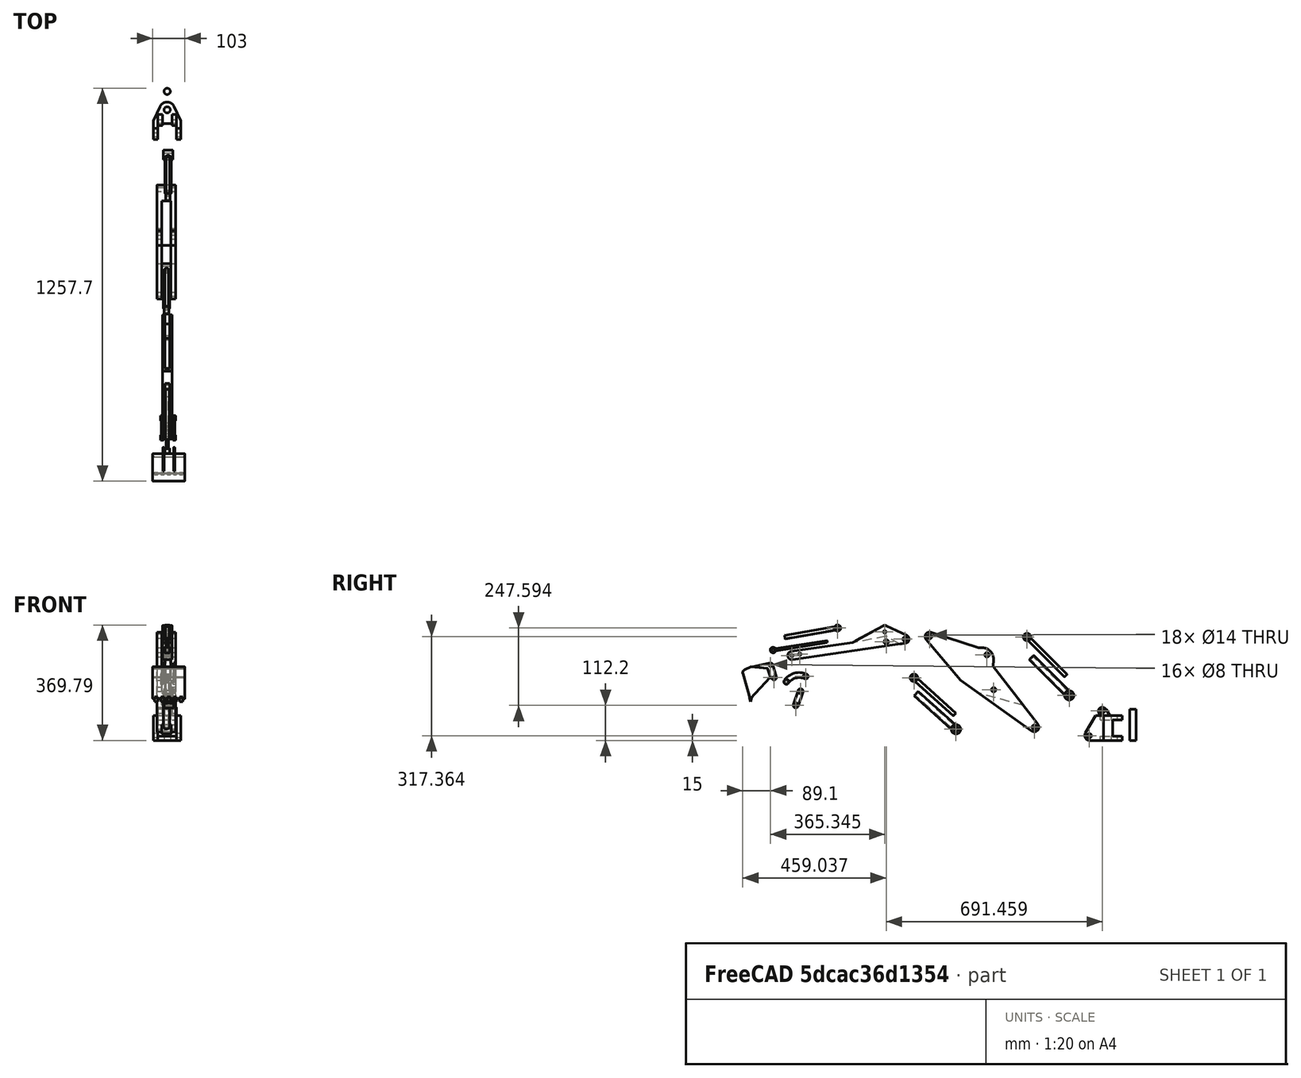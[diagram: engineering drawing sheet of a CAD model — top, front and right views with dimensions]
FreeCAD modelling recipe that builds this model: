
FCSTD DOCUMENT  (FreeCAD 1.0R39319 (Git))
Label: brazo-hidraulico
License: CC-BY 4.0
LicenseURL: https://creativecommons.org/licenses/by/4.0/
objects: App::FeaturePython×17, Part::Feature×13, App::Link×13, App::DocumentObjectGroup×1, Assembly::JointGroup×1, Assembly::AssemblyObject×1
note: 13 computed .brp shape members not serialized (recipe doc carries the construction recipe); baked Part::Feature solids carry a one-line shape summary decoded from their .brp

FEATURE [Part::Feature] Shape001  label="Base"
  shape: bbox 88 x 119.5 x 106 mm, 44 faces (baked)
FEATURE [Part::Feature] Shape012  label="BasePin"
  shape: bbox 20 x 20 x 100 mm, 3 faces (baked)
FEATURE [Part::Feature] Shape013  label="Stick"
  shape: bbox 30 x 388.4 x 109.8 mm, 24 faces (baked)
FEATURE [Part::Feature] Shape014  label="BucketLink1"
  shape: bbox 30 x 31.36 x 61.47 mm, 22 faces (baked)
FEATURE [Part::Feature] Shape015  label="Bucket"
  shape: bbox 103 x 108.6 x 124 mm, 97 faces (baked)
FEATURE [Part::Feature] Shape016  label="BoomCylinderInner"
  shape: bbox 15 x 140.2 x 140.2 mm, 6 faces (baked)
FEATURE [Part::Feature] Shape017  label="StickCylinderInner"
  shape: bbox 15 x 146.3 x 133.8 mm, 6 faces (baked)
FEATURE [Part::Feature] Shape018  label="BucketCylinderInner"
  shape: bbox 15 x 182.7 x 39.88 mm, 6 faces (baked)
FEATURE [Part::Feature] Shape019  label="BucketLink2"
  shape: bbox 48 x 78 x 37.57 mm, 23 faces (baked)
FEATURE [Part::Feature] Shape020  label="BoomCylinderOuter"
  shape: bbox 30 x 143 x 143 mm, 8 faces (baked)
FEATURE [Part::Feature] Shape021  label="StickCylinderOuter"
  shape: bbox 30 x 148.8 x 136.9 mm, 8 faces (baked)
FEATURE [Part::Feature] Shape022  label="BucketCylinderOuter"
  shape: bbox 15 x 179.4 x 45.6 mm, 10 faces (baked)
FEATURE [Part::Feature] Shape  label="Boom"
  shape: bbox 60 x 364 x 319 mm, 31 faces (baked)
FEATURE [App::DocumentObjectGroup] Group  label="CAD"
  Group = -> [Shape001,Shape012,Shape013,Shape014,Shape015,Shape016,Shape017,Shape018,Shape019,Shape020,Shape021,Shape022,Shape]
FEATURE [App::Link] BasePin  label="BasePin001"
  LinkPlacement = pos=(-206.517,40.2557,364.268) rot=(0,0,1;0rad)
  LinkedObject = -> Shape012
  Placement = pos=(-206.517,40.2557,364.268) rot=(0,0,1;0rad)
FEATURE [App::Link] Base  label="Base001"
  LinkPlacement = pos=(-206.517,99.4157,364.268) rot=(0,0,-1;0.004633rad)
  LinkedObject = -> Shape001
  Placement = pos=(-206.517,99.4157,364.268) rot=(0,0,-1;0.004633rad)
FEATURE [App::Link] Boom  label="Boom001"
  LinkPlacement = pos=(-202.932,230.97,229.247) rot=(-0.999947,0.002316,-0.010058;0.452746rad)
  LinkedObject = -> Shape
  Placement = pos=(-202.932,230.97,229.247) rot=(-0.999947,0.002316,-0.010058;0.452746rad)
FEATURE [App::Link] Stick  label="Stick001"
  LinkPlacement = pos=(-205.469,390.408,208.421) rot=(-0.999934,0.002316,-0.011244;0.406359rad)
  LinkedObject = -> Shape013
  Placement = pos=(-205.469,390.408,208.421) rot=(-0.999934,0.002316,-0.011244;0.406359rad)
FEATURE [App::Link] Bucket  label="Bucket001"
  LinkPlacement = pos=(-210.075,432.194,196.62) rot=(-0.99995,0.002316,-0.009747;0.466683rad)
  LinkedObject = -> Shape015
  Placement = pos=(-210.075,432.194,196.62) rot=(-0.99995,0.002316,-0.009747;0.466683rad)
FEATURE [App::Link] BucketLink2  label="BucketLink003"
  LinkPlacement = pos=(-215.535,-1246.73,276.477) rot=(0.999997,-0.002316,0.001009;3.9632rad)
  LinkedObject = -> Shape019
  Placement = pos=(-215.535,-1246.73,276.477) rot=(0.999997,-0.002316,0.001009;3.9632rad)
FEATURE [App::Link] BucketLink1  label="BucketLink004"
  LinkPlacement = pos=(-212.089,-2.4321,-20.3863) rot=(-0.999989,0.002316,-0.004149;1.01849rad)
  LinkedObject = -> Shape014
  Placement = pos=(-212.089,-2.4321,-20.3863) rot=(-0.999989,0.002316,-0.004149;1.01849rad)
FEATURE [App::Link] BoomCylinderOuter  label="BoomCylinderOuter001"
  LinkPlacement = pos=(-209.106,136.254,268.963) rot=(-0.999935,0.002316,-0.011152;0.409629rad)
  LinkedObject = -> Shape020
  Placement = pos=(-209.106,136.254,268.963) rot=(-0.999935,0.002316,-0.011152;0.409629rad)
FEATURE [App::Link] BoomCylinderInner  label="BoomCylinderInner001"
  LinkPlacement = pos=(-208.727,108.582,238.805) rot=(-0.999935,0.002316,-0.011152;0.409629rad)
  LinkedObject = -> Shape016
  Placement = pos=(-208.727,108.582,238.805) rot=(-0.999935,0.002316,-0.011152;0.409629rad)
FEATURE [App::Link] StickCylinderInner  label="StickCylinderInner001"
  LinkPlacement = pos=(-203.709,310.952,236.711) rot=(-0.999971,0.002316,-0.007276;0.616456rad)
  LinkedObject = -> Shape017
  Placement = pos=(-203.709,310.952,236.711) rot=(-0.999971,0.002316,-0.007276;0.616456rad)
FEATURE [App::Link] StickCylinderOuter  label="StickCylinderOuter001"
  LinkPlacement = pos=(-203.027,347.623,221.922) rot=(-0.999971,0.002316,-0.007276;0.616456rad)
  LinkedObject = -> Shape021
  Placement = pos=(-203.027,347.623,221.922) rot=(-0.999971,0.002316,-0.007276;0.616456rad)
FEATURE [App::Link] BucketCylinderInner  label="BucketCylinderInner001"
  LinkPlacement = pos=(-205.355,395.972,110.555) rot=(-0.999962,0.002316,-0.008436;0.535995rad)
  LinkedObject = -> Shape018
  Placement = pos=(-205.355,395.972,110.555) rot=(-0.999962,0.002316,-0.008436;0.535995rad)
FEATURE [App::Link] BucketCylinderOuter  label="BucketCylinderOuter001"
  LinkPlacement = pos=(-205.403,417.48,46.5045) rot=(-0.999964,0.002316,-0.008156;0.553448rad)
  LinkedObject = -> Shape022
  Placement = pos=(-205.403,417.48,46.5045) rot=(-0.999964,0.002316,-0.008156;0.553448rad)
FEATURE [App::FeaturePython] GroundedJoint  # Assembly grounded joint (typed FeaturePython)
  ObjectToGround = -> BasePin
  Placement = pos=(-206.517,40.2557,364.268) rot=(0,0,1;0rad)
FEATURE [App::FeaturePython] Revolute  # Assembly joint (typed FeaturePython)
  Activated = true
  AngleMax = 0
  AngleMin = 0
  Detach1 = false
  Detach2 = false
  Distance = 0
  Distance2 = 0
  EnableAngleMax = false
  EnableAngleMin = false
  EnableLengthMax = false
  EnableLengthMin = false
  JointType = 1 (Revolute)
  LengthMax = 0
  LengthMin = 0
  Placement1 = pos=(0,59.16,0) rot=(0,0,1;1.5708rad)
  Placement2 = pos=(0,0,0) rot=(0.707107,0.707107,0;3.14159rad)
  Reference1 = -> Assembly [BasePin.Face1,BasePin.Edge2]
  Reference2 = -> Assembly [Base.Edge107,Base.Edge107]
FEATURE [App::FeaturePython] Revolute001  # Assembly joint (typed FeaturePython)
  Activated = true
  AngleMax = 45
  AngleMin = -45
  Detach1 = false
  Detach2 = false
  Distance = 0
  Distance2 = 0
  EnableAngleMax = true
  EnableAngleMin = true
  EnableLengthMax = false
  EnableLengthMin = false
  JointType = 1 (Revolute)
  LengthMax = 0
  LengthMin = 0
  Placement1 = pos=(-32.9758,-255.877,42.3644) rot=(0.57735,0.57735,0.57735;2.0944rad)
  Placement2 = pos=(-30,-80,15) rot=(-0.57735,-0.57735,0.57735;2.0944rad)
  Reference1 = -> Assembly [Boom.Face1,Boom.Edge5]
  Reference2 = -> Assembly [Base.Edge61,Base.Edge61]
FEATURE [App::FeaturePython] Revolute002  # Assembly joint (typed FeaturePython)
  Activated = true
  AngleMax = 0
  AngleMin = 0
  Detach1 = false
  Detach2 = false
  Distance = 0
  Distance2 = 0
  EnableAngleMax = false
  EnableAngleMin = false
  EnableLengthMax = false
  EnableLengthMin = false
  JointType = 1 (Revolute)
  LengthMax = 0
  LengthMin = 0
  Placement1 = pos=(-12.24,-144.25,144.25) rot=(0.678598,0.281085,0.678598;2.59356rad)
  Placement2 = pos=(-15,-38.0444,94.4593) rot=(0.57735,-0.57735,0.57735;4.18879rad)
  Reference1 = -> Assembly [BoomCylinderOuter.Edge8,BoomCylinderOuter.Edge8]
  Reference2 = -> Assembly [Base.Edge34,Base.Edge34]
FEATURE [App::FeaturePython] Slider  # Assembly joint (typed FeaturePython)
  Activated = true
  AngleMax = 0
  AngleMin = 0
  Detach1 = false
  Detach2 = false
  Distance = 0
  Distance2 = 0
  EnableAngleMax = false
  EnableAngleMin = false
  EnableLengthMax = true
  EnableLengthMin = false
  JointType = 3 (Slider)
  LengthMax = 80
  LengthMin = 52.0086
  Placement1 = pos=(2.252,-213.159,265.212) rot=(0,-0.382683,0.92388;3.14159rad)
  Placement2 = pos=(2.76,-265.165,265.165) rot=(0,-0.382683,0.92388;3.14159rad)
  Reference1 = -> Assembly [BoomCylinderInner.Face1,BoomCylinderInner.Face1]
  Reference2 = -> Assembly [BoomCylinderOuter.Face1,BoomCylinderOuter.Edge3]
FEATURE [App::FeaturePython] Cylindrical  # Assembly joint (typed FeaturePython)
  Activated = true
  AngleMax = 0
  AngleMin = 0
  Detach1 = false
  Detach2 = false
  Distance = 0
  Distance2 = 0
  EnableAngleMax = false
  EnableAngleMin = false
  EnableLengthMax = false
  EnableLengthMin = false
  JointType = 2 (Cylindrical)
  LengthMax = 0
  LengthMin = 0
  Placement1 = pos=(-5.248,-279.1,331.153) rot=(0.678598,-0.281085,0.678598;3.68962rad)
  Placement2 = pos=(-17.9758,-407.377,273.864) rot=(0.57735,0.57735,-0.57735;4.18879rad)
  Reference1 = -> Assembly [BoomCylinderInner.Edge7,BoomCylinderInner.Edge7]
  Reference2 = -> Assembly [Boom.Edge53,Boom.Edge53]
FEATURE [App::FeaturePython] Revolute003  # Assembly joint (typed FeaturePython)
  Activated = true
  AngleMax = -23
  AngleMin = -48
  Detach1 = false
  Detach2 = false
  Distance = 0
  Distance2 = 0
  EnableAngleMax = true
  EnableAngleMin = true
  EnableLengthMax = false
  EnableLengthMin = false
  JointType = 1 (Revolute)
  LengthMax = 0
  LengthMin = 0
  Placement1 = pos=(12.66,-506.596,35.8372) rot=(0.682415,0.261954,0.682415;2.6292rad)
  Placement2 = pos=(12.0242,-385.877,162.364) rot=(0.57735,0.57735,-0.57735;4.18879rad)
  Reference1 = -> Assembly [StickCylinderOuter.Face2,StickCylinderOuter.Edge3]
  Reference2 = -> Assembly [Boom.Edge66,Boom.Edge66]
FEATURE [App::FeaturePython] Slider001  # Assembly joint (typed FeaturePython)
  Activated = true
  AngleMax = 0
  AngleMin = 0
  Detach1 = false
  Detach2 = false
  Distance = 0
  Distance2 = 0
  EnableAngleMax = false
  EnableAngleMin = false
  EnableLengthMax = true
  EnableLengthMin = false
  JointType = 3 (Slider)
  LengthMax = 80
  LengthMin = 63.2772
  Placement1 = pos=(-1.828,-571.574,138.121) rot=(0,-0.406737,0.913545;3.14159rad)
  Placement2 = pos=(-2.34,-633.674,150.259) rot=(0,-0.406737,0.913545;3.14159rad)
  Reference1 = -> Assembly [StickCylinderInner.Face1,StickCylinderInner.Face1]
  Reference2 = -> Assembly [StickCylinderOuter.Face6,StickCylinderOuter.Edge3]
FEATURE [App::FeaturePython] Revolute004  # Assembly joint (typed FeaturePython)
  Activated = true
  AngleMax = 0
  AngleMin = 0
  Detach1 = false
  Detach2 = false
  Distance = 0
  Distance2 = 0
  EnableAngleMax = false
  EnableAngleMin = false
  EnableLengthMax = false
  EnableLengthMin = false
  JointType = 1 (Revolute)
  LengthMax = 0
  LengthMin = 0
  Placement1 = pos=(-14.7,-729.503,315.527) rot=(0.363936,0.85738,0.363936;1.72407rad)
  Placement2 = pos=(-17.9758,-590.877,332.364) rot=(0.57735,0.57735,-0.57735;4.18879rad)
  Reference1 = -> Assembly [Stick.Edge41,Stick.Edge41]
  Reference2 = -> Assembly [Boom.Edge51,Boom.Edge51]
FEATURE [App::FeaturePython] Cylindrical001  # Assembly joint (typed FeaturePython)
  Activated = true
  AngleMax = 0
  AngleMin = 0
  Detach1 = false
  Detach2 = false
  Distance = 0
  Distance2 = 0
  EnableAngleMax = false
  EnableAngleMin = false
  EnableLengthMax = false
  EnableLengthMin = false
  JointType = 2 (Cylindrical)
  LengthMax = 0
  LengthMin = 0
  Placement1 = pos=(-7.2,-669.12,324.36) rot=(0.363936,0.85738,0.363936;1.72407rad)
  Placement2 = pos=(-9.328,-640.876,200.52) rot=(0.674471,-0.300294,0.674471;3.72505rad)
  Reference1 = -> Assembly [Stick.Edge57,Stick.Edge57]
  Reference2 = -> Assembly [StickCylinderInner.Face4,StickCylinderInner.Face4]
FEATURE [App::FeaturePython] Revolute005  # Assembly joint (typed FeaturePython)
  Activated = true
  AngleMax = -120
  AngleMin = -145
  Detach1 = false
  Detach2 = false
  Distance = 0
  Distance2 = 0
  EnableAngleMax = true
  EnableAngleMin = true
  EnableLengthMax = false
  EnableLengthMin = false
  JointType = 1 (Revolute)
  LengthMax = 0
  LengthMin = 0
  Placement1 = pos=(-7.14,-885.253,359.794) rot=(0.705758,-0.061746,0.705758;3.26493rad)
  Placement2 = pos=(-7.2,-734.095,347.625) rot=(0.363936,0.85738,0.363936;1.72407rad)
  Reference1 = -> Assembly [BucketCylinderOuter.Face6,BucketCylinderOuter.Face6]
  Reference2 = -> Assembly [Stick.Edge56,Stick.Edge56]
FEATURE [App::FeaturePython] Slider002  # Assembly joint (typed FeaturePython)
  Activated = true
  AngleMax = 0
  AngleMin = 0
  Detach1 = false
  Detach2 = false
  Distance = 0
  Distance2 = 0
  EnableAngleMax = false
  EnableAngleMin = false
  EnableLengthMax = true
  EnableLengthMin = false
  JointType = 3 (Slider)
  LengthMax = 0
  LengthMin = 0
  Placement1 = pos=(0.212,-1000.72,303.69) rot=(0,-0.760406,0.649448;3.14159rad)
  Placement2 = pos=(0.36,-974.049,344.137) rot=(0,-0.766044,0.642788;3.14159rad)
  Reference1 = -> Assembly [BucketCylinderInner.Face1,BucketCylinderInner.Face1]
  Reference2 = -> Assembly [BucketCylinderOuter.Face1,BucketCylinderOuter.Face1]
FEATURE [App::FeaturePython] Revolute006  # Assembly joint (typed FeaturePython)
  Activated = true
  AngleMax = 0
  AngleMin = 0
  Detach1 = false
  Detach2 = false
  Distance = 0
  Distance2 = 0
  EnableAngleMax = false
  EnableAngleMin = false
  EnableLengthMax = false
  EnableLengthMin = false
  JointType = 1 (Revolute)
  LengthMax = 0
  LengthMin = 0
  Placement1 = pos=(-12.2189,-987.052,204.816) rot=(-0.707107,0,-0.707107;3.14159rad)
  Placement2 = pos=(-14.7,-1006.04,276.188) rot=(0.363936,0.85738,0.363936;1.72407rad)
  Reference1 = -> Assembly [BucketLink2.Edge49,BucketLink2.Edge49]
  Reference2 = -> Assembly [Stick.Face20,Stick.Edge10]
FEATURE [App::FeaturePython] Revolute007  # Assembly joint (typed FeaturePython)
  Activated = true
  AngleMax = 0
  AngleMin = 0
  Detach1 = false
  Detach2 = false
  Distance = 0
  Distance2 = 0
  EnableAngleMax = false
  EnableAngleMin = false
  EnableLengthMax = false
  EnableLengthMin = false
  JointType = 1 (Revolute)
  LengthMax = 0
  LengthMin = 0
  Placement1 = pos=(-9.9,-1088.34,200.94) rot=(0.57735,0.57735,0.57735;2.0944rad)
  Placement2 = pos=(-14.7,-1031.22,271.858) rot=(0.363936,0.85738,0.363936;1.72407rad)
  Reference1 = -> Assembly [Bucket.Edge139,Bucket.Edge139]
  Reference2 = -> Assembly [Stick.Face20,Stick.Edge6]
FEATURE [App::FeaturePython] Revolute008  # Assembly joint (typed FeaturePython)
  Activated = true
  AngleMax = 0
  AngleMin = 0
  Detach1 = false
  Detach2 = false
  Distance = 0
  Distance2 = 0
  EnableAngleMax = false
  EnableAngleMin = false
  EnableLengthMax = false
  EnableLengthMin = false
  JointType = 1 (Revolute)
  LengthMax = 0
  LengthMin = 0
  Placement1 = pos=(-9.9,-1018.98,112.2) rot=(0.57735,0.57735,0.57735;2.0944rad)
  Placement2 = pos=(-9.9,-1099.44,240.39) rot=(0.57735,0.57735,0.57735;2.0944rad)
  Reference1 = -> Assembly [BucketLink1.Face11,BucketLink1.Face11]
  Reference2 = -> Assembly [Bucket.Face65,Bucket.Edge2]
FEATURE [App::FeaturePython] Cylindrical002  # Assembly joint (typed FeaturePython)
  Activated = true
  AngleMax = 0
  AngleMin = 0
  Detach1 = false
  Detach2 = false
  Distance = 0
  Distance2 = 0
  EnableAngleMax = false
  EnableAngleMin = false
  EnableLengthMax = false
  EnableLengthMin = false
  JointType = 2 (Cylindrical)
  LengthMax = 0
  LengthMin = 0
  Placement1 = pos=(-2.9,-1003.62,157.675) rot=(0.57735,0.57735,0.57735;2.0944rad)
  Placement2 = pos=(2.78108,-1049.05,187.816) rot=(-0.57735,-0.57735,-0.57735;4.18879rad)
  Reference1 = -> Assembly [BucketLink1.Edge25,BucketLink1.Edge25]
  Reference2 = -> Assembly [BucketLink2.Face13,BucketLink2.Face13]
FEATURE [App::FeaturePython] Cylindrical003  # Assembly joint (typed FeaturePython)
  Activated = true
  AngleMax = 0
  AngleMin = 0
  Detach1 = false
  Detach2 = false
  Distance = 0
  Distance2 = 0
  EnableAngleMax = false
  EnableAngleMin = false
  EnableLengthMax = false
  EnableLengthMin = false
  JointType = 2 (Cylindrical)
  LengthMax = 0
  LengthMin = 0
  Placement1 = pos=(0.211998,-1091.57,289.302) rot=(0.544663,-0.637718,0.544663;4.27698rad)
  Placement2 = pos=(2.78108,-1049.05,187.816) rot=(-0.57735,-0.57735,-0.57735;4.18879rad)
  Reference1 = -> Assembly [BucketCylinderInner.Face3,BucketCylinderInner.Face3]
  Reference2 = -> Assembly [BucketLink2.Face13,BucketLink2.Face13]
FEATURE [Assembly::JointGroup] Joints
  Group = -> [GroundedJoint,Revolute,Revolute001,Revolute002,Slider,Cylindrical,Revolute003,Slider001,Revolute004,Cylindrical001,Revolute005,Slider002,Revolute006,Revolute007,Revolute008,Cylindrical002,Cylindrical003]
FEATURE [Assembly::AssemblyObject] Assembly
  Group = -> [Joints,BasePin,Base,Boom,Stick,Bucket,BucketLink2,BucketLink1,BoomCylinderOuter,BoomCylinderInner,StickCylinderInner,StickCylinderOuter,BucketCylinderInner,BucketCylinderOuter,GroundedJoint,Revolute,Revolute001,Revolute002,Slider,Cylindrical,Revolute003,Slider001,Revolute004,Cylindrical001,Revolute005,Slider002,Revolute006,Revolute007,Revolute008,Cylindrical002,Cylindrical003]
  Origin = -> Origin
  Type = Assembly
